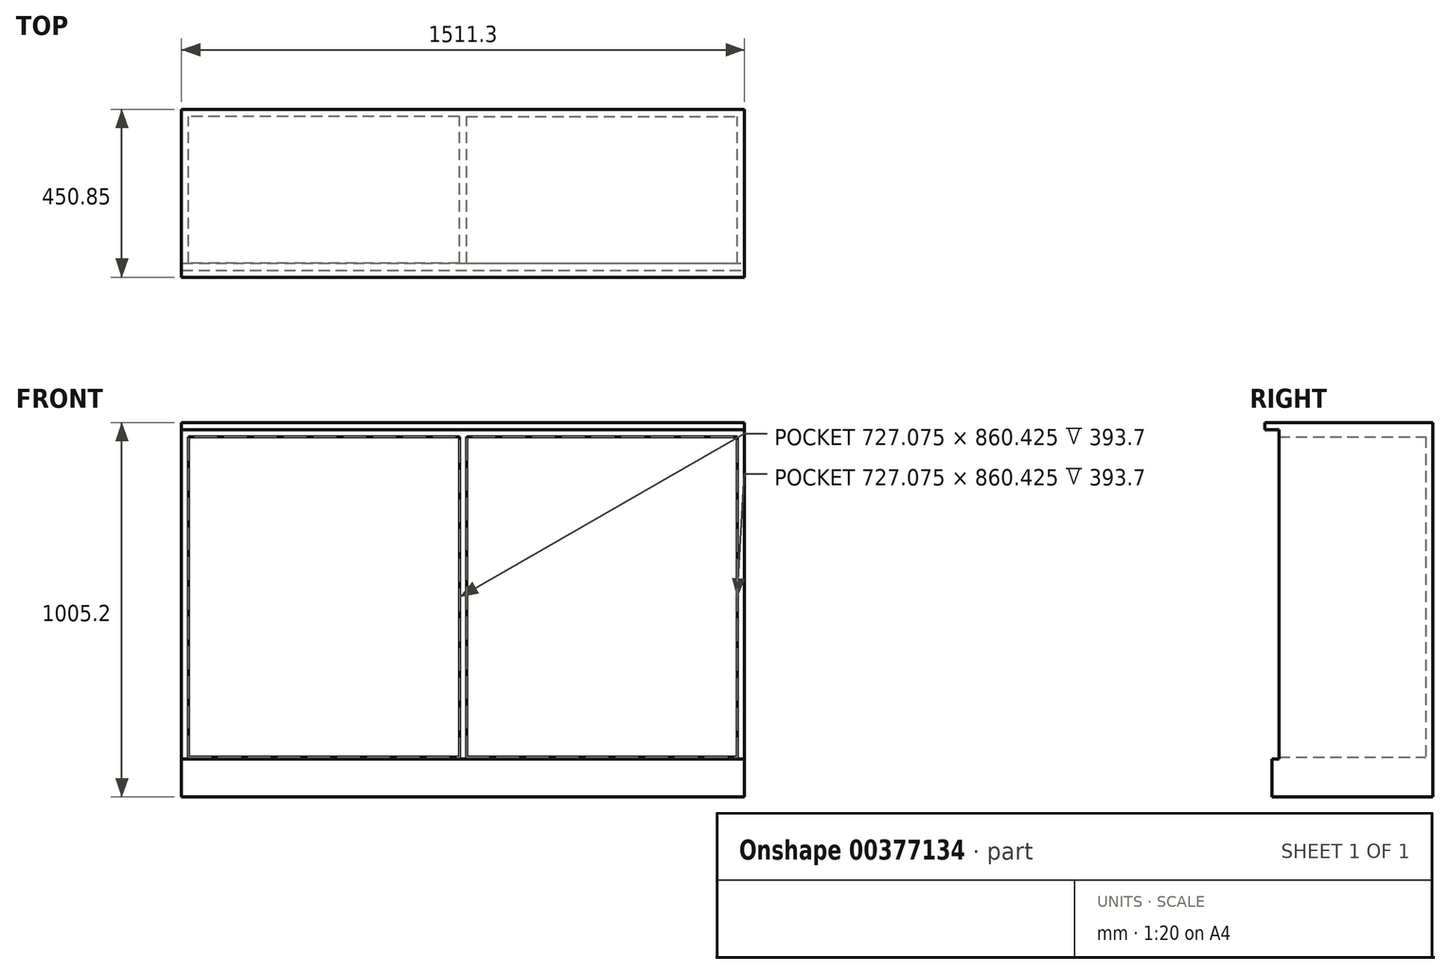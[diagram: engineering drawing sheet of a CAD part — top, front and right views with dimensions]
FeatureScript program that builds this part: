
annotation { "Feature Type Name" : "Feature", "Feature Type Description" : "" }
export const myFeature = defineFeature(function(context is Context, id is Id, definition is map)
    precondition{}
    {
        {
            var Q0;
            Q0=qCreatedBy(makeId("Front.planeOp"),FACE);
            var sketch = newSketch(context, id + "F0", { "sketchPlane" : qUnion([Q0])});
            skLineSegment(sketch, "E0", {"start": v(0, 0) * mm, "end": v(0, 860.42) * mm, "construction": true});
            skLineSegment(sketch, "E1", {"start": v(0, 860.42) * mm, "end": v(736.6, 860.42) * mm});
            skLineSegment(sketch, "E2", {"start": v(736.6, 860.43) * mm, "end": v(736.6, 0) * mm});
            skLineSegment(sketch, "E3", {"start": v(736.6, 0) * mm, "end": v(0, 0) * mm});
            skLineSegment(sketch, "E4.MirrorCS", {"start": v(0, 860.42) * mm, "end": v(-736.6, 860.42) * mm});
            skLineSegment(sketch, "E5.MirrorCS", {"start": v(-736.6, 860.43) * mm, "end": v(-736.6, 0) * mm});
            skLineSegment(sketch, "E6.MirrorCS", {"start": v(-736.6, 0) * mm, "end": v(0, 0) * mm});
            skLineSegment(sketch, "E7", {"start": v(9.52, 860.42) * mm, "end": v(9.53, 0) * mm});
            skLineSegment(sketch, "E8", {"start": v(736.6, 860.43) * mm, "end": v(755.65, 860.43) * mm});
            skLineSegment(sketch, "E9", {"start": v(755.65, 860.43) * mm, "end": v(755.65, 0) * mm});
            skLineSegment(sketch, "E10", {"start": v(755.65, 0) * mm, "end": v(736.6, 0) * mm});
            skLineSegment(sketch, "E11", {"start": v(0, 860.42) * mm, "end": v(0, 879.48) * mm});
            skLineSegment(sketch, "E12", {"start": v(0, 879.48) * mm, "end": v(755.65, 879.48) * mm});
            skLineSegment(sketch, "E13", {"start": v(755.65, 879.48) * mm, "end": v(755.65, 860.43) * mm});
            skLineSegment(sketch, "E14.MirrorCS", {"start": v(0, 879.48) * mm, "end": v(-755.65, 879.47) * mm});
            skLineSegment(sketch, "E15.MirrorCS", {"start": v(-9.52, 860.42) * mm, "end": v(-9.53, 0) * mm});
            skLineSegment(sketch, "E16.MirrorCS", {"start": v(-755.65, 860.43) * mm, "end": v(-755.65, 0) * mm});
            skLineSegment(sketch, "E17.MirrorCS", {"start": v(-755.65, 879.48) * mm, "end": v(-755.65, 860.43) * mm});
            skLineSegment(sketch, "E18.MirrorCS", {"start": v(-755.65, 0) * mm, "end": v(-736.6, 0) * mm});
            skLineSegment(sketch, "E19.MirrorCS", {"start": v(-736.6, 860.42) * mm, "end": v(-755.65, 860.42) * mm});
            skLineSegment(sketch, "E20", {"start": v(-755.65, 0) * mm, "end": v(-755.65, -5.08) * mm});
            skLineSegment(sketch, "E21", {"start": v(-755.65, -5.08) * mm, "end": v(755.65, -5.08) * mm});
            skLineSegment(sketch, "E22", {"start": v(755.65, -5.08) * mm, "end": v(755.65, 0) * mm});
            skSolve(sketch);
        }
        {
            var Q0;
            Q0 = qSketchRegion(id + "F0", true);
            var Q1;
            {var subQ4=sQuery(id+"F0.wireOp",EDGE,"E7");Q1=makeQuery(id+"F0.imprint","IMPRINT",FACE,{"disambiguationData":[TD([[makeQuery(id+"F0.imprint","IMPRINT",EDGE,{"derivedFrom":subQ4}),-1.0]])]});}
            extrude(context, id + "F1", {"entities" : qUnion([Q0, Q1]), "depth" : 393.7 * mm});
        }
        {
            var Q0;
            Q0=makeQuery(id+"F1.opExtrude","CAP_FACE",FACE,{"disambiguationData":[OSD([sQuery(id+"F0.wireOp",EDGE,"E1"),sQuery(id+"F0.wireOp",EDGE,"E2"),sQuery(id+"F0.wireOp",EDGE,"E3"),sQuery(id+"F0.wireOp",EDGE,"E4.MirrorCS"),sQuery(id+"F0.wireOp",EDGE,"E5.MirrorCS"),sQuery(id+"F0.wireOp",EDGE,"E6.MirrorCS"),sQuery(id+"F0.wireOp",EDGE,"E7"),sQuery(id+"F0.wireOp",EDGE,"E9"),sQuery(id+"F0.wireOp",EDGE,"E12"),sQuery(id+"F0.wireOp",EDGE,"E13"),sQuery(id+"F0.wireOp",EDGE,"E14.MirrorCS"),sQuery(id+"F0.wireOp",EDGE,"E15.MirrorCS"),sQuery(id+"F0.wireOp",EDGE,"E16.MirrorCS"),sQuery(id+"F0.wireOp",EDGE,"E17.MirrorCS"),sQuery(id+"F0.wireOp",EDGE,"E20"),sQuery(id+"F0.wireOp",EDGE,"E21"),sQuery(id+"F0.wireOp",EDGE,"E22")])],"isStart":true});
            var sketch = newSketch(context, id + "F2", { "sketchPlane" : qUnion([Q0])});
            skLineSegment(sketch, "E23.0", {"start": v(755.65, 879.48) * mm, "end": v(-755.65, 879.48) * mm});
            skLineSegment(sketch, "E24.0", {"start": v(-755.65, 879.48) * mm, "end": v(-755.65, -5.08) * mm});
            skLineSegment(sketch, "E25.0", {"start": v(755.65, -5.08) * mm, "end": v(-755.65, -5.08) * mm});
            skLineSegment(sketch, "E26.0", {"start": v(755.65, 879.47) * mm, "end": v(755.65, -5.08) * mm});
            skSolve(sketch);
        }
        {
            var Q0;
            Q0 = qSketchRegion(id + "F2", true);
            extrude(context, id + "F3", {"entities" : qUnion([Q0]), "operationType" : NewBodyOperationType.ADD, "depth" : 19.05 * mm});
        }
        {
            var Q0;
            Q0=makeQuery(id+"F3.boolean.opBoolean","MERGE",FACE,{"derivedFrom":[makeQuery(id+"F1.opExtrude","SWEPT_FACE",FACE,{"disambiguationData":[OSD([sQuery(id+"F0.wireOp",EDGE,"E12"),sQuery(id+"F0.wireOp",EDGE,"E14.MirrorCS")])]}),makeQuery(id+"F3.opExtrude","SWEPT_FACE",FACE,{"disambiguationData":[OSD([sQuery(id+"F2.wireOp",EDGE,"E23.0")])]})]});
            var sketch = newSketch(context, id + "F4", { "sketchPlane" : qUnion([Q0])});
            skLineSegment(sketch, "E27", {"start": v(-755.65, 19.05) * mm, "end": v(755.65, 19.05) * mm});
            skLineSegment(sketch, "E28", {"start": v(755.65, 19.05) * mm, "end": v(755.65, -431.8) * mm});
            skLineSegment(sketch, "E29", {"start": v(755.65, -431.8) * mm, "end": v(-755.65, -431.8) * mm});
            skLineSegment(sketch, "E30", {"start": v(-755.65, -431.8) * mm, "end": v(-755.65, 19.05) * mm});
            skSolve(sketch);
        }
        {
            var Q0;
            Q0 = qSketchRegion(id + "F4", true);
            extrude(context, id + "F5", {"entities" : qUnion([Q0]), "operationType" : NewBodyOperationType.ADD, "depth" : 19.05 * mm});
        }
        {
            var Q0;
            Q0=makeQuery(id+"F3.boolean.opBoolean","MERGE",FACE,{"derivedFrom":[makeQuery(id+"F1.opExtrude","SWEPT_FACE",FACE,{"disambiguationData":[OSD([sQuery(id+"F0.wireOp",EDGE,"E21")])]}),makeQuery(id+"F3.opExtrude","SWEPT_FACE",FACE,{"disambiguationData":[OSD([sQuery(id+"F2.wireOp",EDGE,"E25.0")])]})]});
            var sketch = newSketch(context, id + "F6", { "sketchPlane" : qUnion([Q0])});
            skLineSegment(sketch, "E31.bottom", {"start": v(-755.65, -19.05) * mm, "end": v(755.65, -19.05) * mm});
            skLineSegment(sketch, "E31.top", {"start": v(-755.65, 412.75) * mm, "end": v(755.65, 412.75) * mm});
            skLineSegment(sketch, "E31.left", {"start": v(-755.65, -19.05) * mm, "end": v(-755.65, 412.75) * mm});
            skLineSegment(sketch, "E31.right", {"start": v(755.65, -19.05) * mm, "end": v(755.65, 412.75) * mm});
            skSolve(sketch);
        }
        {
            var Q0;
            Q0 = qSketchRegion(id + "F6", true);
            extrude(context, id + "F7", {"entities" : qUnion([Q0]), "operationType" : NewBodyOperationType.ADD, "depth" : 101.6 * mm});
        }
    });
